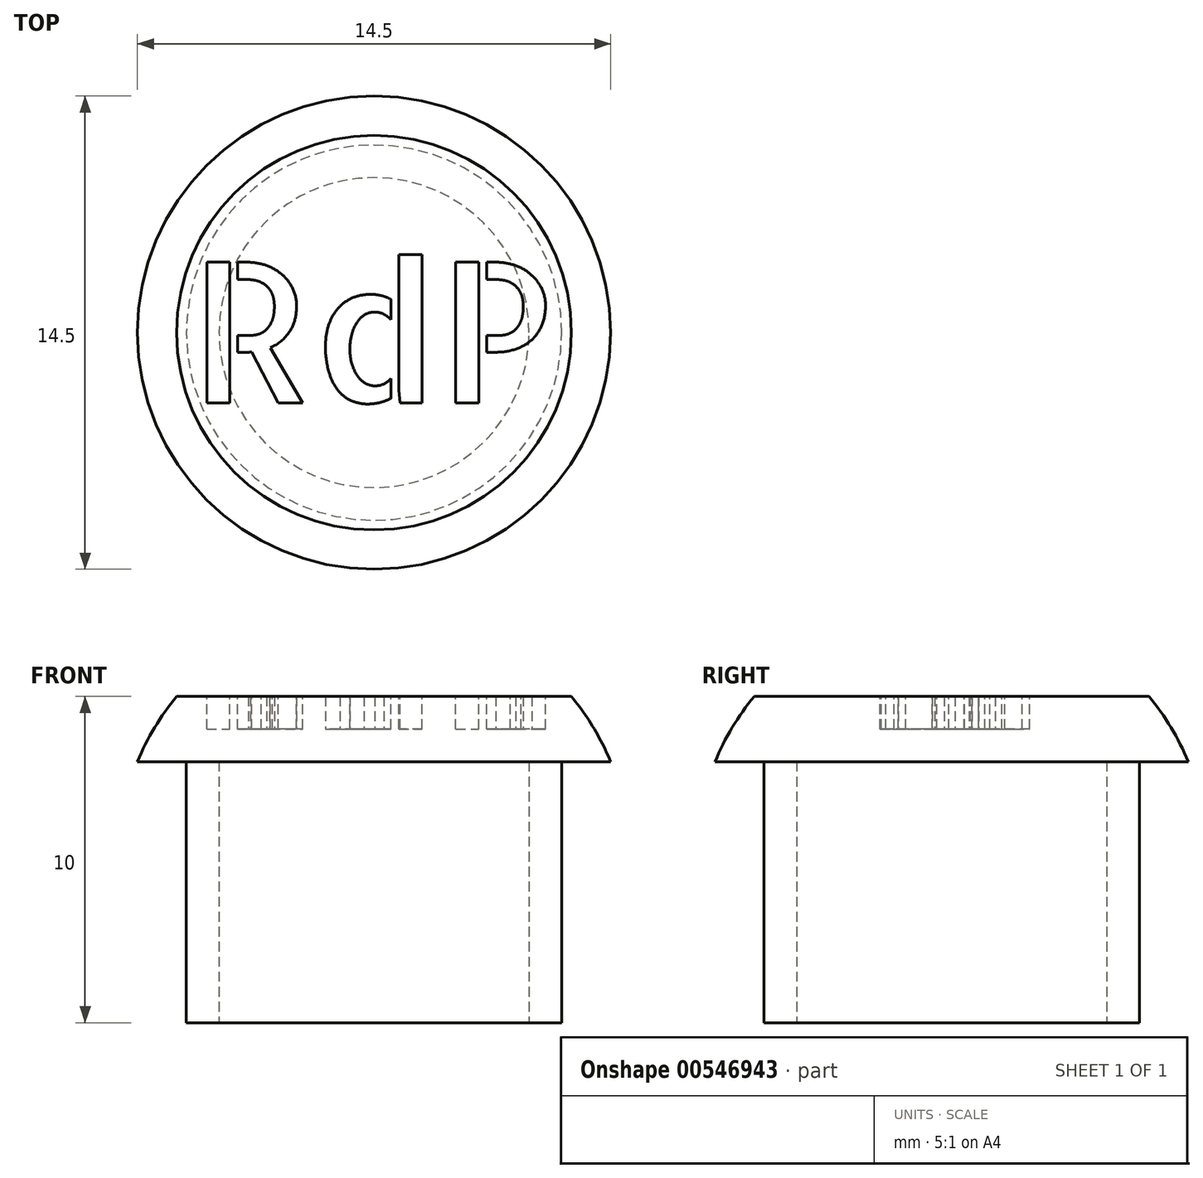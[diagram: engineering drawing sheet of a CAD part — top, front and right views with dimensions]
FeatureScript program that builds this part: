
annotation { "Feature Type Name" : "Feature", "Feature Type Description" : "" }
export const myFeature = defineFeature(function(context is Context, id is Id, definition is map)
    precondition{}
    {
        {
            var Q0;
            Q0=qCreatedBy(makeId("Top.planeOp"),FACE);
            var sketch = newSketch(context, id + "F0", { "sketchPlane" : qUnion([Q0])});
            skCircle(sketch, "E0", {"center": v(0, 0) * mm, "radius": 5.75 * mm});
            skCircle(sketch, "E1.0", {"center": v(0, 0) * mm, "radius": 4.75 * mm});
            skSolve(sketch);
        }
        {
            var Q0;
            Q0=makeQuery(id+"F0.imprint","IMPRINT",FACE,{"disambiguationData":[TD([[makeQuery(id+"F0.imprint","IMPRINT",EDGE,{"derivedFrom":sQuery(id+"F0.wireOp",EDGE,"E0")}),1.0]])]});
            extrude(context, id + "F1", {"entities" : qUnion([Q0]), "depth" : 8 * mm, "offsetDistance" : 25 * mm});
        }
        {
            var Q0;
            Q0=qCreatedBy(makeId("Front.planeOp"),FACE);
            var sketch = newSketch(context, id + "F2", { "sketchPlane" : qUnion([Q0])});
            skLineSegment(sketch, "E2", {"start": v(0, 0) * mm, "end": v(0, 8) * mm});
            skLineSegment(sketch, "E3", {"start": v(0, 8) * mm, "end": v(5.75, 8) * mm});
            skLineSegment(sketch, "E4", {"start": v(5.75, 8) * mm, "end": v(7.25, 8) * mm});
            skArc(sketch, "E5", {"start": v(7.25, 8) * mm, "mid": v(6.72, 9.04) * mm, "end": v(6.05, 10) * mm});
            skLineSegment(sketch, "E6", {"start": v(0, 8) * mm, "end": v(0, 10) * mm});
            skLineSegment(sketch, "E7", {"start": v(0, 10) * mm, "end": v(6.05, 10) * mm});
            skSolve(sketch);
        }
        {
            var Q0;
            Q0=makeQuery(id+"F2.imprint","IMPRINT",FACE,{"disambiguationData":[TD([[makeQuery(id+"F2.imprint","IMPRINT",EDGE,{"derivedFrom":sQuery(id+"F2.wireOp",EDGE,"E3")}),1.0]])]});
            var Q1;
            Q1=sQuery(id+"F2.wireOp",EDGE,"E2");
            revolve(context, id + "F3", {"operationType" : NewBodyOperationType.ADD, "entities" : qUnion([Q0]), "axis" : qUnion([Q1]), "revolveType" : RevolveType.FULL, "oppositeDirection" : true});
        }
        {
            var Q0;
            Q0=makeQuery(id+"F3.opRevolve","SWEPT_FACE",FACE,{"disambiguationData":[OSD([sQuery(id+"F2.wireOp",EDGE,"E7")])]});
            var sketch = newSketch(context, id + "F4", { "sketchPlane" : qUnion([Q0])});
            skText(sketch, "E8", { "text": "RdP", "fontName": "AllertaStencil-Regular.ttf"});
            const initialGuessF4  = {"E8": [-0.00565, -0.00216, 1, 0, 0.00432]};
            skSetInitialGuess(sketch, initialGuessF4);
            skSolve(sketch);
        }
        {
            var Q0;
            Q0=qSketchRegion(id+"F4",true);
            extrude(context, id + "F5", {"entities" : qUnion([Q0]), "operationType" : NewBodyOperationType.REMOVE, "oppositeDirection" : true, "depth" : 1 * mm, "offsetDistance" : 25 * mm});
        }
    });
